# Revit family: Vandal Proof Batten_240V_Ceiling-Hosted R16
name_source: partatom
category: Lighting Fixtures
revit_build: Autodesk Revit 2016 (Build: 20150220_1215(x64)
units: mm (PartAtom-declared; Revit-internal decimal feet)

## family parameters
Always vertical = Yes
Cut with Voids When Loaded = No
Host = Ceiling
Light Source = Yes
OmniClass Number = 23.80.70.11
OmniClass Title = Luminaries for Internal Lighting
Part Type = Normal
Room Calculation Point = No
Round Connector Dimension = Use Diameter
Shared = No
Work Plane-Based = No

## types (2) — shared parameters
Ceiling = <By Category>
Color Filter = 16777215
Construction = Pressure Die-Cast, Low Copper Aluminium Alloy Body with Grey P/Coat, Removable Gear Tray & ReplaceableLED Modules
Diffuser = Opal, Impact Resistant Polycarbonate with Secure Access Screws
Dimensions = 1320 x 140 x 120mm (L x W x H)
Dimming Lamp Color Temperature Shift = <None>
Emit Shape Visible in Rendering = No
Emit from Circle Diameter = 610 mm
IK Rating = IK10
IP Rating = IP66
Lamp = 2 x LED module, 4000K natural white, 50,000h [L80/B20, Ta40C], Ra>80
Mounting = Surface Mount
Operating Temperature = 0C to 40C
Operating Voltage = 240C AC; 50Hz
Photometric Web File = 6035_FVP4LED-P_350mA_ProductionDiffuser_18082017-01_Revised.ies
Power Consumption = 43W
Tilt Angle = 60.00°

## per-type parameters (varying)
| type | Driver/Ballast | Product Description |
| FVPLED-P | Tridonic LC 50W 350-1050mA | 240V 4ft Argonaut LED Vandal Batten |
| FVP4LED-P-DD | Tridonic LC 50W 350-1050mA ONE4ALL | 240V 4ft Argonaut LED Vandal Batten with DALI Driver |

## geometry (parser evidence)
native form markers: Sweep x3
no freeform markers — native parametric forms only
